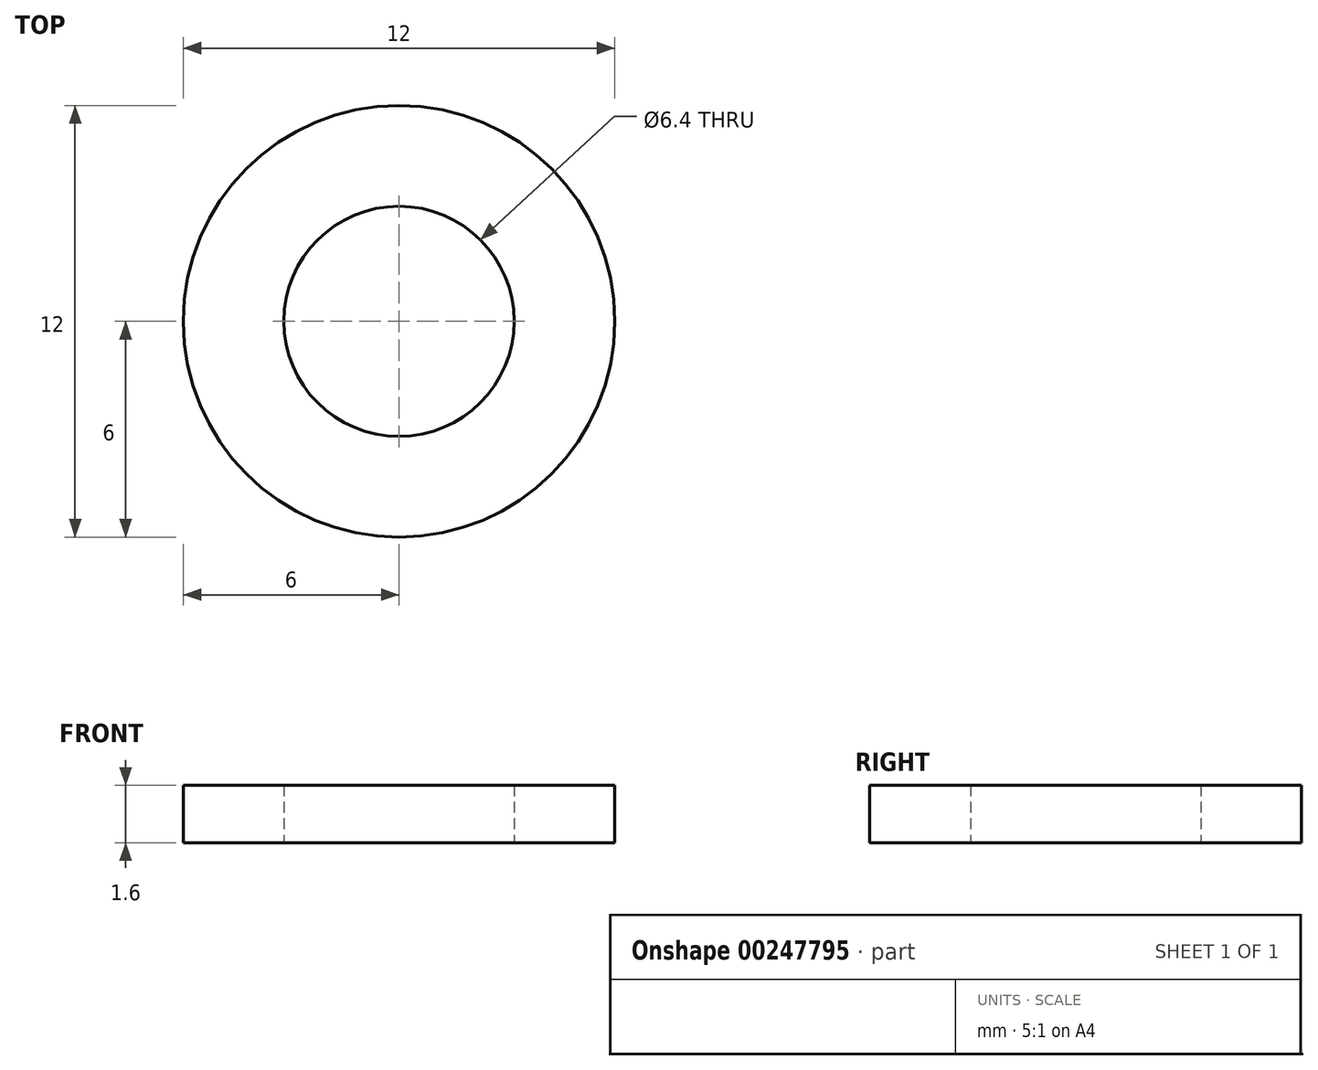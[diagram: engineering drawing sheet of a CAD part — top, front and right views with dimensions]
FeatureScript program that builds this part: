
annotation { "Feature Type Name" : "Feature", "Feature Type Description" : "" }
export const myFeature = defineFeature(function(context is Context, id is Id, definition is map)
    precondition{}
    {
        {
            var Q0;
            Q0=qCreatedBy(makeId("Top.planeOp"),FACE);
            var sketch = newSketch(context, id + "F0", { "sketchPlane" : qUnion([Q0])});
            skCircle(sketch, "E0", {"center": v(0, 0) * mm, "radius": 3.2 * mm});
            skCircle(sketch, "E1", {"center": v(0, 0) * mm, "radius": 6 * mm});
            skSolve(sketch);
        }
        {
            var Q0;
            Q0=qSketchRegion(id+"F0",true);
            extrude(context, id + "F1", {"entities" : qUnion([Q0]), "depth" : 1.6 * mm});
        }
    });
